# Revit family: KEUCO_59545010101
name_source: partatom
category: Allgemeines Modell
revit_build: Autodesk Revit 2016 (Build: 20150220_1215(x64)
units: mm (PartAtom-declared; Revit-internal decimal feet)

## family parameters
Arbeitsebenenbasiert = Ja
Beim Laden mit Abzugskörper schneiden = Nein
Bemaßung runder Anschluss = Durchmesser verwenden
Gemeinsam genutzt = Nein
Immer vertikal = Nein
Kann Basisbauteil für Bewehrung sein = Nein
Raumberechnungspunkt = Nein
Teiletyp = Normal

## types (1)
- 59545010101
    Artikelnummer = 59545010101
    Ausschreibungstext = KEUCO IXMO Wanneneinlauf DN 15, 59545010101,
hochglanzverchromter Wanneneinlauf DN 15 
in zeitloser Formensprache, 
passend für alle Unterputz-Armaturen, 
runde Rosett mit 90 mm Durchmesser, 
Gesamtausladung 202 mm, Wasseraustritt bei 180 mm, 
Wasseranschluss G 1/2 Zoll, Durchmesser 35 mm, 
empfohlene Funktionseinheit: 59547000170 
in Kombination mit Montageschiene 5957000001-3
    Beschreibung = mit runder Rosette,
passend für alle UP-Armaturen
    Breite = 202 mm  [stored 0.66273 ft]
    Gewicht = 0
    Hersteller = KEUCO
    Material = Stahl, verchromt
    Serie = Plan
    URL = https://www.keuco.com
    Verwendung = DU / WA
    Vorgabe-Ansicht = 1219 mm

note: [stored X ft] marks values corroborated as IEEE doubles in the binary element streams (Revit-internal decimal feet)

## geometry (parser evidence)
native form markers: Sweep x3
no freeform markers — native parametric forms only
